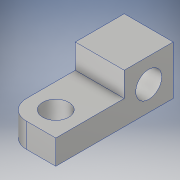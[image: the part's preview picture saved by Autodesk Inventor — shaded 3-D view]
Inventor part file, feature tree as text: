
AUTODESK INVENTOR PART (.ipt)
format: ipt  version: 2018 (Build 220112000, 112)  size: 153,600 bytes
history: native  units: in
note: dims shown in document units (in); Inventor stores cm internally (conversion verified against a paired STEP export)
features: sketch x4, extrude x2, hole x2, fillet x1
ambient origin geometry x8: Origin, YZ Plane, XZ Plane, XY Plane, X Axis, Y Axis, Z Axis, Center Point
bodies: Solid1 (feature_tree)
feature tree (9):
  extrude  "Extrusion1"  Depth=1.2in
  hole  "Hole1"  [1 undecoded]
  hole  "Hole2"  [1 undecoded]
  extrude  "Extrusion2"  Depth=0.25in
  fillet  "Fillet2"  Radius=0.5in
  sketch  "Sketch1"  dims[d0=0.5in d1=1.2in]
  sketch  "Sketch2"  dims[d2=0.5in d3=0.0in]
  sketch  "Sketch3"  dims[d5=0.266in d6=0.75in d7=0.507in d8=0.25in d9=0.5635in d10=1.0in d11=0.8108in d12=0.25in]
  sketch  "Sketch4"  dims[d13=0.25in d14=90.0deg d15=0.266in d16=0.75in d17=0.507in d18=0.25in d19=0.5635in d20=1.0in d21=0.8108in d23=0.25in d24=0.5in d25=0.0in d27=0.25in d28=0.5in d30=0.2in]
note: 2 required parameter values undecoded (feature->parameter linkage not recoverable at this tier; creation-order binding heuristic only, values carry confidence <= 0.55)
